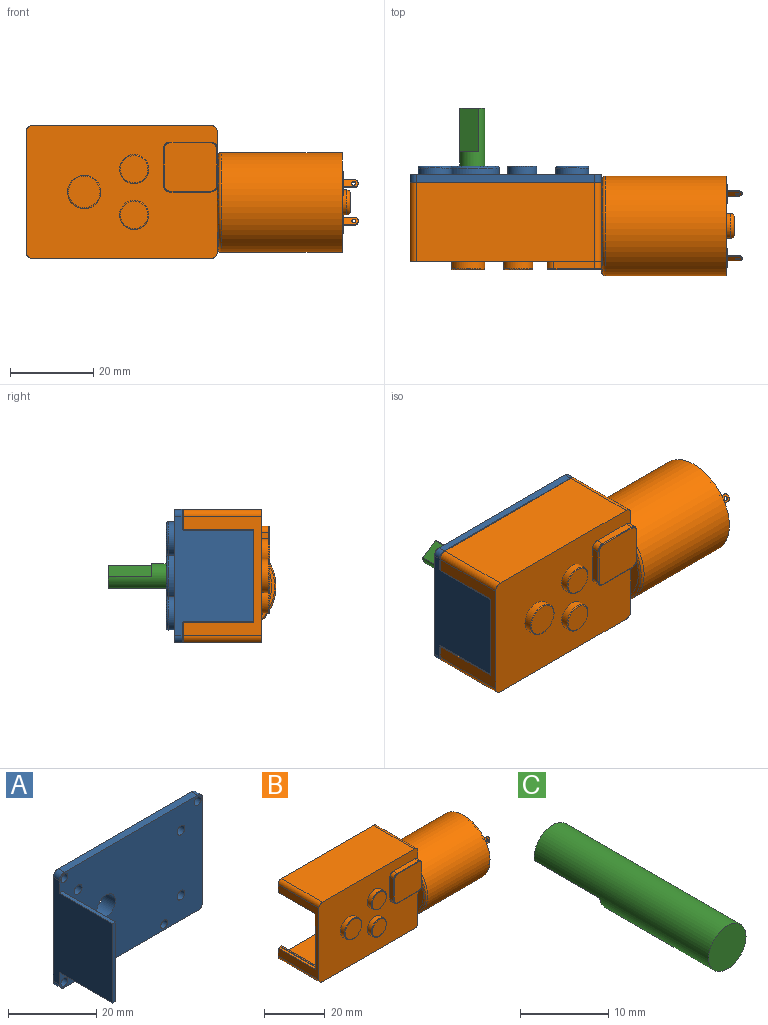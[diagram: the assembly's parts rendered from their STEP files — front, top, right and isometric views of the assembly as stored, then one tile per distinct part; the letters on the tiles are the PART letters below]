
ASSEMBLY  parts=3 mates=2
PART A: 46 faces, bbox 46x21x32 mm
  f0: cylinder r=6.5mm len=13mm, axis (0,-1,0), area 65.3mm2, adj f1,f7
  f1: torus R=6.1mm, axis (0,1,0), area 25.1mm2, adj f0,f44
  f2: plane 46x32mm, normal (0,-1,0), area 1384.7mm2, adj f3,f4,f5,f6,f10,f14,f22,f24
  f3: plane 28.8x19mm, normal (-1,0,0), area 431.6mm2, adj f2,f7,f34,f35,f36,f38,f39
  f4: plane 42.8x2mm, normal (0,0,1), area 85.6mm2, adj f2,f7,f33,f35
  f5: plane 28.8x2mm, normal (1,0,0), area 57.6mm2, adj f2,f7,f32,f33
  f6: plane 42.8x2mm, normal (0,0,-1), area 85.6mm2, adj f2,f7,f32,f34
  f7: plane 46x32mm, normal (0,1,0), area 1043.8mm2, adj f0,f3,f4,f5,f6,f8,f12,f16
  f8: cylinder r=4mm len=8mm, axis (0,-1,0), area 40.2mm2, adj f7,f43
  f9: plane 7.2x7.2mm, normal (0,1,0), area 33.4mm2, adj f11,f43
  f10: cylinder r=1.25mm len=3.73mm, axis (0,1,0), area 29.3mm2, adj f2,f11
  f11: cone r=1.53mm half-angle=45deg, axis (0,1,0), area 3.4mm2, adj f9,f10
  f12: cylinder r=4mm len=8mm, axis (0,-1,0), area 40.2mm2, adj f7,f42
  f13: plane 7.2x7.2mm, normal (0,1,0), area 33.4mm2, adj f15,f42
  f14: cylinder r=1.25mm len=3.73mm, axis (0,1,0), area 29.3mm2, adj f2,f15
  f15: cone r=1.53mm half-angle=45deg, axis (0,1,0), area 3.4mm2, adj f13,f14
  f16: cylinder r=3.5mm len=7mm, axis (0,-1,0), area 44mm2, adj f7,f17
  f17: plane 7x7mm, normal (0,1,0), area 38.5mm2, adj f16
  f18: cylinder r=4mm len=8mm, axis (0,-1,0), area 40.2mm2, adj f7,f41
  f19: plane 7.2x7.2mm, normal (0,1,0), area 33.4mm2, adj f23,f41
  f20: cylinder r=4mm len=8mm, axis (0,-1,0), area 40.2mm2, adj f7,f40
  f21: plane 7.2x7.2mm, normal (0,1,0), area 33.4mm2, adj f25,f40
  f22: cylinder r=1.25mm len=3.73mm, axis (0,1,0), area 29.3mm2, adj f2,f23
  f23: cone r=1.53mm half-angle=45deg, axis (0,1,0), area 3.4mm2, adj f19,f22
  f24: cylinder r=1.25mm len=3.73mm, axis (0,1,0), area 29.3mm2, adj f2,f25
  f25: cone r=1.53mm half-angle=45deg, axis (0,1,0), area 3.4mm2, adj f21,f24
  f26: cylinder r=3.5mm len=7mm, axis (0,-1,0), area 44mm2, adj f7,f27
  f27: plane 7x7mm, normal (0,1,0), area 38.5mm2, adj f26
  f28: cylinder r=1.1mm len=2.2mm, axis (0,1,0), area 13.8mm2, adj f2,f7
  f29: cylinder r=1.1mm len=2.2mm, axis (0,1,0), area 13.8mm2, adj f2,f7
  f30: cylinder r=1.1mm len=2.2mm, axis (0,1,0), area 13.8mm2, adj f2,f7
  f31: cylinder r=1.1mm len=2.2mm, axis (0,1,0), area 13.8mm2, adj f2,f7
  f32: cylinder r=1.6mm len=2mm, axis (0,-1,0), area 5mm2, adj f2,f5,f6,f7
  f33: cylinder r=1.6mm len=2mm, axis (0,-1,0), area 5mm2, adj f2,f4,f5,f7
  f34: cylinder r=1.6mm len=2mm, axis (0,-1,0), area 5mm2, adj f2,f3,f6,f7
  f35: cylinder r=1.6mm len=2mm, axis (0,-1,0), area 5mm2, adj f2,f3,f4,f7
  f36: plane 17x1mm, normal (0,0,-1), area 17mm2, adj f2,f3,f37,f39
  f37: plane 22x17mm, normal (1,0,0), area 374mm2, adj f2,f36,f38,f39
  f38: plane 17x1mm, normal (0,0,1), area 17mm2, adj f2,f3,f37,f39
  f39: plane 22x1mm, normal (0,-1,0), area 22mm2, adj f3,f36,f37,f38
  f40: torus R=3.6mm, axis (0,1,0), area 15.2mm2, adj f20,f21
  f41: torus R=3.6mm, axis (0,1,0), area 15.2mm2, adj f18,f19
  f42: torus R=3.6mm, axis (0,1,0), area 15.2mm2, adj f12,f13
  f43: torus R=3.6mm, axis (0,1,0), area 15.2mm2, adj f8,f9
  f44: plane 12.2x12.2mm, normal (0,1,0), area 88.6mm2, adj f1,f45
  f45: cylinder r=3mm len=6mm, axis (0,-1,0), area 75.4mm2, adj f2,f44
PART B: 127 faces, bbox 79.8x26x32 mm
  f0: plane 20.8x13.62mm, normal (1,0,0), area 157.2mm2, adj f3,f7,f32,f34,f37,f44,f121
  f1: plane 19x8.62mm, normal (1,0,0), area 49.1mm2, adj f3,f7,f31,f121
  f2: plane 17.2x1.4mm, normal (1,0,0), area 24.1mm2, adj f3,f55,f58,f59
  f3: plane 46x32mm, normal (0,1,0), area 204.1mm2, adj f0,f1,f2,f4,f5,f6,f10,f13
  f4: plane 28.8x19mm, normal (-1,0,0), area 161.9mm2, adj f3,f7,f30,f33,f58,f62,f64
  f5: plane 42.8x19mm, normal (0,0,-1), area 813.2mm2, adj f3,f7,f30,f31
  f6: plane 42.8x19mm, normal (0,0,1), area 813.2mm2, adj f3,f7,f32,f33
  f7: plane 46x32mm, normal (0,-1,0), area 1188.8mm2, adj f0,f1,f4,f5,f6,f20,f22,f24
  f8: cone r=0.8mm half-angle=59deg, axis (0,1,0), area 2.3mm2, adj f9
  f9: cylinder r=0.8mm len=5.78mm, axis (0,1,0), area 29mm2, adj f8,f10
  f10: cone r=1.03mm half-angle=45deg, axis (0,1,0), area 1.8mm2, adj f3,f9
  f11: cone r=0.8mm half-angle=59deg, axis (0,1,0), area 2.3mm2, adj f12
  f12: cylinder r=0.8mm len=5.78mm, axis (0,1,0), area 29mm2, adj f11,f13
  f13: cone r=1.03mm half-angle=45deg, axis (0,1,0), area 1.8mm2, adj f3,f12
  f14: cone r=0.8mm half-angle=59deg, axis (0,1,0), area 2.3mm2, adj f15
  f15: cylinder r=0.8mm len=5.78mm, axis (0,1,0), area 29mm2, adj f14,f16
  f16: cone r=1.03mm half-angle=45deg, axis (0,1,0), area 1.8mm2, adj f3,f15
  f17: cone r=0.8mm half-angle=59deg, axis (0,1,0), area 2.3mm2, adj f18
  f18: cylinder r=0.8mm len=5.78mm, axis (0,1,0), area 29mm2, adj f17,f19
  f19: cone r=1.03mm half-angle=45deg, axis (0,1,0), area 1.8mm2, adj f3,f18
  f20: cylinder r=4mm len=8mm, axis (0,1,0), area 45.2mm2, adj f7,f48
  f21: plane 7.6x7.6mm, normal (0,-1,0), area 45.4mm2, adj f48
  f22: cylinder r=3.5mm len=7mm, axis (0,1,0), area 39.6mm2, adj f7,f47
  f23: plane 6.6x6.6mm, normal (0,-1,0), area 34.2mm2, adj f47
  f24: cylinder r=3.5mm len=7mm, axis (0,1,0), area 39.6mm2, adj f7,f46
  f25: plane 6.6x6.6mm, normal (0,-1,0), area 34.2mm2, adj f46
  f26: plane 8.8x1.8mm, normal (-1,0,0), area 15.8mm2, adj f7,f35,f36,f39
  f27: plane 9.8x1.8mm, normal (0,0,-1), area 17.6mm2, adj f7,f36,f37,f43
  f28: plane 9.8x1.8mm, normal (0,0,1), area 17.6mm2, adj f7,f34,f35,f40
  f29: plane 12.6x11.6mm, normal (0,-1,0), area 144.5mm2, adj f38,f39,f40,f41,f42,f43,f44,f45
  f30: cylinder r=1.6mm len=19mm, axis (0,1,0), area 47.8mm2, adj f3,f4,f5,f7
  f31: cylinder r=1.6mm len=19mm, axis (0,1,0), area 47.8mm2, adj f1,f3,f5,f7
  f32: cylinder r=1.6mm len=19mm, axis (0,1,0), area 47.8mm2, adj f0,f3,f6,f7
  f33: cylinder r=1.6mm len=19mm, axis (0,1,0), area 47.8mm2, adj f3,f4,f6,f7
  f34: cylinder r=1.6mm len=1.8mm, axis (0,1,0), area 4.5mm2, adj f0,f7,f28,f42
  f35: cylinder r=1.6mm len=1.8mm, axis (0,1,0), area 4.5mm2, adj f7,f26,f28,f38
  f36: cylinder r=1.6mm len=1.8mm, axis (0,1,0), area 4.5mm2, adj f7,f26,f27,f41
  f37: cylinder r=1.6mm len=1.8mm, axis (0,1,0), area 4.5mm2, adj f0,f7,f27,f45,f126
  f38: torus R=1.4mm, axis (0,1,0), area 0.8mm2, adj f29,f35,f39,f40
  f39: cylinder r=0.2mm len=8.8mm, axis (0,0,-1), area 2.8mm2, adj f26,f29,f38,f41
  f40: cylinder r=0.2mm len=9.8mm, axis (-1,0,0), area 3.1mm2, adj f28,f29,f38,f42
  f41: torus R=1.4mm, axis (0,1,0), area 0.8mm2, adj f29,f36,f39,f43
  f42: torus R=1.4mm, axis (0,1,0), area 0.8mm2, adj f29,f34,f40,f44
  f43: cylinder r=0.2mm len=9.8mm, axis (1,0,0), area 3.1mm2, adj f27,f29,f41,f45
  f44: cylinder r=0.2mm len=8.8mm, axis (0,0,1), area 2.8mm2, adj f0,f29,f42,f45
  f45: torus R=1.4mm, axis (0,1,0), area 0.8mm2, adj f29,f37,f43,f44
  f46: torus R=3.3mm, axis (0,-1,0), area 6.8mm2, adj f24,f25
  f47: torus R=3.3mm, axis (0,-1,0), area 6.8mm2, adj f22,f23
  f48: torus R=3.8mm, axis (0,-1,0), area 7.8mm2, adj f20,f21
  f49: plane 17.2x8.8mm, normal (0,0,1), area 151.4mm2, adj f3,f50,f57,f58
  f50: plane 26.8x17.2mm, normal (-1,0,0), area 432.7mm2, adj f3,f49,f51,f58,f65
  f51: cylinder r=2mm len=17.2mm, axis (0,1,0), area 54mm2, adj f3,f50,f52,f58
  f52: plane 38.8x17.2mm, normal (0,0,-1), area 667.4mm2, adj f3,f51,f53,f58
  f53: cylinder r=2mm len=17.2mm, axis (0,1,0), area 54mm2, adj f3,f52,f54,f58
  f54: plane 17.2x1.4mm, normal (1,0,0), area 24.1mm2, adj f3,f53,f58,f60
  f55: cylinder r=2mm len=17.2mm, axis (0,1,0), area 54mm2, adj f2,f3,f56,f58
  f56: plane 28x17.2mm, normal (0,0,1), area 481.6mm2, adj f3,f55,f57,f58
  f57: cylinder r=2mm len=17.2mm, axis (0,1,0), area 108.1mm2, adj f3,f49,f56,f58
  f58: plane 44.4x28.8mm, normal (0,1,0), area 1252.5mm2, adj f2,f4,f49,f50,f51,f52,f53,f54
  f59: plane 17.2x0.6mm, normal (0,0,1), area 10.3mm2, adj f2,f3,f58,f63
  f60: plane 17.2x0.6mm, normal (0,0,-1), area 10.3mm2, adj f3,f54,f58,f61
  f61: plane 17.2x0.2mm, normal (-1,0,0), area 3.4mm2, adj f3,f58,f60,f62
  f62: plane 17.2x1mm, normal (0,0,-1), area 17.2mm2, adj f3,f4,f58,f61
  f63: plane 17.2x0.2mm, normal (-1,0,0), area 3.4mm2, adj f3,f58,f59,f64
  f64: plane 17.2x1mm, normal (0,0,1), area 17.2mm2, adj f3,f4,f58,f63
  f65: cylinder r=3mm len=6mm, axis (1,0,0), area 30.2mm2, adj f50,f68
  f66: plane 2x2mm, normal (-1,0,0), area 3.1mm2, adj f67
  f67: cylinder r=1mm len=10mm, axis (-1,0,0), area 62.8mm2, adj f66,f68
  f68: plane 6x6mm, normal (-1,0,0), area 25.1mm2, adj f65,f67
  f69: plane 6.56x0.5mm, normal (-1,0,0), area 2.2mm2, adj f3,f121
  f70: plane 23.4x23.4mm, normal (1,0,0), area 426.9mm2, adj f71,f75
  f71: cylinder r=1mm len=29mm, axis (-1,0,0), area 182.2mm2, adj f70,f79
  f72: plane 5.83x4.55mm, normal (1,0,0), area 15.4mm2, adj f109,f110,f111,f112,f113,f114,f115,f116
  f73: plane 23.4x23.4mm, normal (1,0,0), area 344.7mm2, adj f78,f80,f83,f84,f85,f86,f87,f88
  f74: plane 5.83x4.55mm, normal (1,0,0), area 15.4mm2, adj f93,f94,f95,f96,f101,f102,f103,f104
  f75: cylinder r=11.7mm len=29mm, axis (1,0,0), area 2131.9mm2, adj f70,f79
  f76: cylinder r=12mm len=29mm, axis (1,0,0), area 2186.5mm2, adj f77,f121
  f77: plane 24x24mm, normal (1,0,0), area 22.3mm2, adj f76,f78
  f78: cylinder r=11.7mm len=23.4mm, axis (1,0,0), area 36.8mm2, adj f73,f77
  f79: plane 23.4x23.4mm, normal (-1,0,0), area 419.8mm2, adj f71,f75,f83,f84,f85,f86,f87,f88
  f80: cylinder r=3mm len=6mm, axis (-1,0,0), area 28.3mm2, adj f73,f82
  f81: plane 4x4mm, normal (1,0,0), area 12.6mm2, adj f82
  f82: torus R=2mm, axis (1,0,0), area 26mm2, adj f80,f81
  f83: cylinder r=0.5mm len=0.91mm, axis (1,0,0), area 0.3mm2, adj f73,f79,f84,f86
  f84: cylinder r=4mm len=1.6mm, axis (1,0,0), area 0.3mm2, adj f73,f79,f83,f85
  f85: cylinder r=0.5mm len=0.99mm, axis (1,0,0), area 0.3mm2, adj f73,f79,f84,f86
  f86: cylinder r=5mm len=2mm, axis (1,0,0), area 0.4mm2, adj f73,f79,f83,f85
  f87: cylinder r=0.5mm len=0.91mm, axis (1,0,0), area 0.3mm2, adj f73,f79,f88,f90
  f88: cylinder r=4mm len=1.6mm, axis (1,0,0), area 0.3mm2, adj f73,f79,f87,f89
  f89: cylinder r=0.5mm len=0.99mm, axis (1,0,0), area 0.3mm2, adj f73,f79,f88,f90
  f90: cylinder r=5mm len=2mm, axis (1,0,0), area 0.4mm2, adj f73,f79,f87,f89
  f91: cylinder r=0.5mm len=1mm, axis (1,0,0), area 0.6mm2, adj f73,f79
  f92: cylinder r=0.5mm len=1mm, axis (1,0,0), area 0.6mm2, adj f73,f79
  f93: cylinder r=1.4mm len=2.61mm, axis (-1,0,0), area 3.5mm2, adj f73,f74,f94,f96
  f94: plane 3.03x1.75mm, normal (0,-0.87,0.5), area 2.8mm2, adj f73,f74,f93,f95
  f95: cylinder r=1.4mm len=2.61mm, axis (-1,0,0), area 3.5mm2, adj f73,f74,f94,f96
  f96: plane 3.03x1.75mm, normal (0,0.87,-0.5), area 2.8mm2, adj f73,f74,f93,f95
  f97: cylinder r=1.2mm len=2.4mm, axis (-1,0,0), area 3mm2, adj f73,f98
  f98: plane 2.4x2.4mm, normal (1,0,0), area 4.5mm2, adj f97
  f99: cylinder r=1.2mm len=2.4mm, axis (-1,0,0), area 3mm2, adj f73,f100
  f100: plane 2.4x2.4mm, normal (1,0,0), area 4.5mm2, adj f99
  f101: plane 2.75x0.26mm, normal (0,-0.5,-0.87), area 0.8mm2, adj f74,f102,f104,f108
  f102: plane 3.5x1.73mm, normal (0,0.87,-0.5), area 6mm2, adj f74,f101,f103,f105,f106,f107,f108
  f103: plane 2.75x0.26mm, normal (0,0.5,0.87), area 0.8mm2, adj f74,f102,f104,f107
  f104: plane 3.5x1.73mm, normal (0,-0.87,0.5), area 6mm2, adj f74,f101,f103,f105,f106,f107,f108
  f105: plane 0.58x0.51mm, normal (1,0,0), area 0.1mm2, adj f102,f104,f107,f108
  f106: cylinder r=0.5mm len=1.02mm, axis (0,-0.87,0.5), area 0.9mm2, adj f102,f104
  f107: cylinder r=0.75mm len=0.8mm, axis (0,0.87,-0.5), area 0.4mm2, adj f102,f103,f104,f105
  f108: cylinder r=0.75mm len=0.8mm, axis (0,-0.87,0.5), area 0.4mm2, adj f101,f102,f104,f105
  f109: cylinder r=1.4mm len=2.61mm, axis (-1,0,0), area 3.5mm2, adj f72,f73,f110,f112
  f110: plane 3.03x1.75mm, normal (0,0.87,-0.5), area 2.8mm2, adj f72,f73,f109,f111
  f111: cylinder r=1.4mm len=2.61mm, axis (-1,0,0), area 3.5mm2, adj f72,f73,f110,f112
  f112: plane 3.03x1.75mm, normal (0,-0.87,0.5), area 2.8mm2, adj f72,f73,f109,f111
  f113: plane 2.75x0.26mm, normal (0,0.5,0.87), area 0.8mm2, adj f72,f114,f116,f120
  f114: plane 3.5x1.73mm, normal (0,-0.87,0.5), area 6mm2, adj f72,f113,f115,f117,f118,f119,f120
  f115: plane 2.75x0.26mm, normal (0,-0.5,-0.87), area 0.8mm2, adj f72,f114,f116,f119
  f116: plane 3.5x1.73mm, normal (0,0.87,-0.5), area 6mm2, adj f72,f113,f115,f117,f118,f119,f120
  f117: plane 0.58x0.51mm, normal (1,0,0), area 0.1mm2, adj f114,f116,f119,f120
  f118: cylinder r=0.5mm len=1.02mm, axis (0,0.87,-0.5), area 0.9mm2, adj f114,f116
  f119: cylinder r=0.75mm len=0.8mm, axis (0,-0.87,0.5), area 0.4mm2, adj f114,f115,f116,f117
  f120: cylinder r=0.75mm len=0.8mm, axis (0,0.87,-0.5), area 0.4mm2, adj f113,f114,f116,f117
  f121: torus R=11mm, axis (1,0,0), area 114.8mm2, adj f0,f1,f69,f76,f126
  f122: cylinder r=1.2mm len=2.4mm, axis (-1,0,0), area 3mm2, adj f73,f123
  f123: plane 2.4x2.4mm, normal (1,0,0), area 4.5mm2, adj f122
  f124: cylinder r=1.2mm len=2.4mm, axis (-1,0,0), area 3mm2, adj f73,f125
  f125: plane 2.4x2.4mm, normal (1,0,0), area 4.5mm2, adj f124
  f126: plane 11.08x2.5mm, normal (-1,0,0), area 21.1mm2, adj f7,f37,f121
PART C: 5 faces, bbox 6x28x6 mm
  f0: cylinder r=3mm len=28mm, axis (0,1,0), area 461.8mm2, adj f1,f2,f3,f4
  f1: plane 6x6mm, normal (0,-1,0), area 28.3mm2, adj f0
  f2: plane 6x5.35mm, normal (0,1,0), area 22.7mm2, adj f0,f3
  f3: plane 10.5x4.83mm, normal (-0.37,0,-0.93), area 54.6mm2, adj f0,f2,f4
  f4: plane 4.83x2.56mm, normal (0,1,0), area 5.5mm2, adj f0,f3
PLACE A t=(-2.18,-1.92,3.85)mm
PLACE B t=(-2.19,-1.72,3.85)mm
PLACE C rot(axis=(0,1,0),127.8deg) t=(-2.18,-1.92,3.85)mm
MATE revolute C.f0 <-> A.f0  axis (0,1,0) through (-2.18,2.08,3.85)mm
MATE fastened A.f39 <-> B.f58  axis (0,-1,0) through (-16.68,-18.92,3.85)mm
